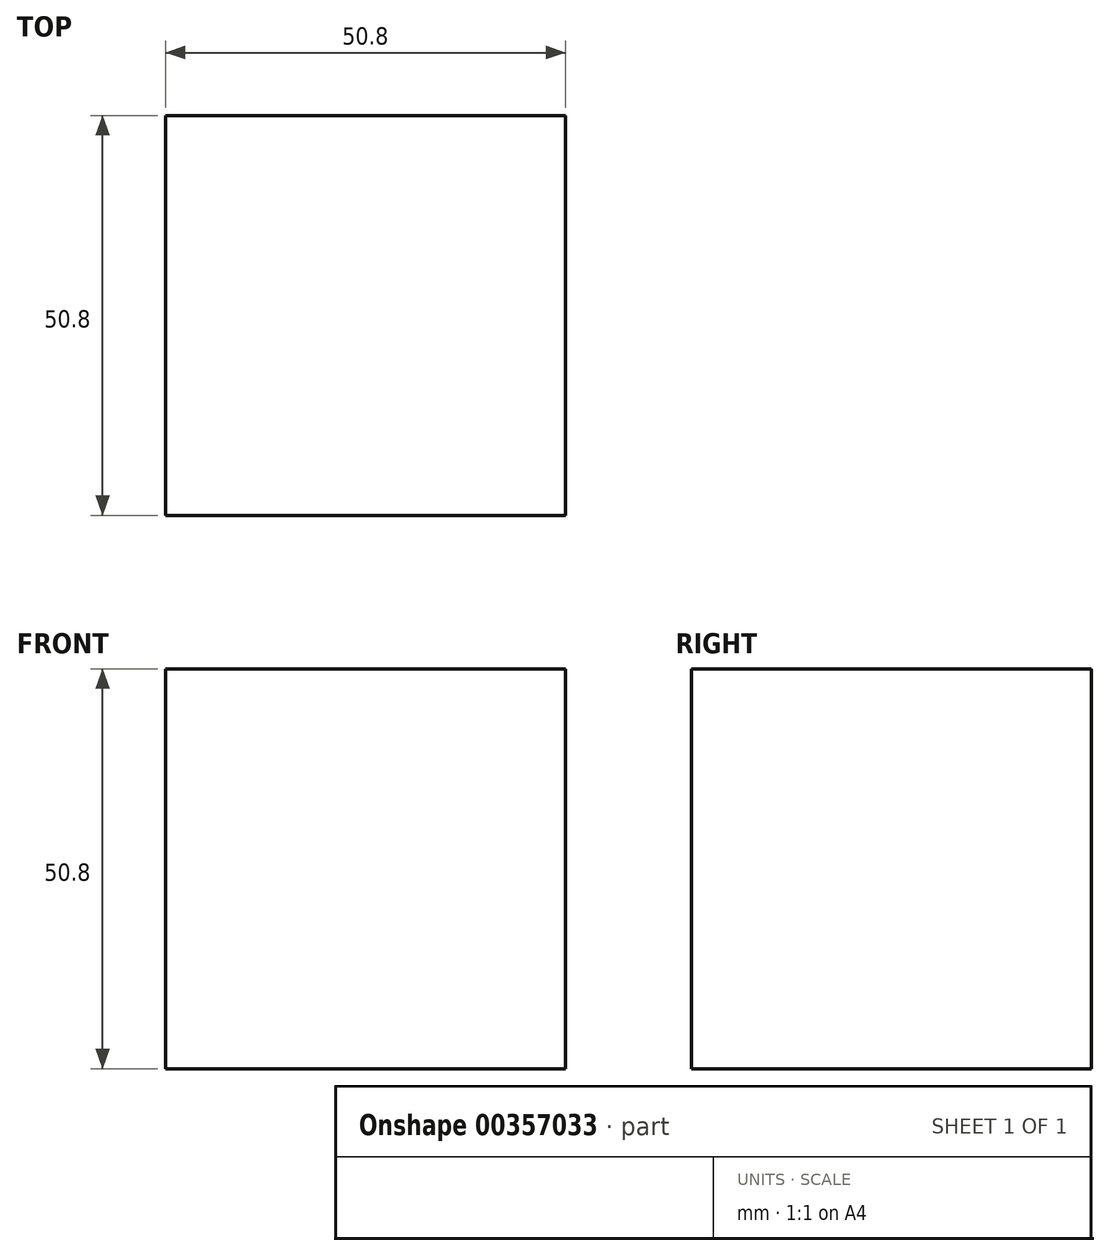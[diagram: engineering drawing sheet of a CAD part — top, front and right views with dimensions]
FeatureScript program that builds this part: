
annotation { "Feature Type Name" : "Feature", "Feature Type Description" : "" }
export const myFeature = defineFeature(function(context is Context, id is Id, definition is map)
    precondition{}
    {
        {
            var Q0;
            Q0=qCreatedBy(makeId("Front.planeOp"),FACE);
            var sketch = newSketch(context, id + "F0", { "sketchPlane" : qUnion([Q0])});
            skLineSegment(sketch, "E0", {"start": v(0, 0) * mm, "end": v(0, 50.8) * mm});
            skLineSegment(sketch, "E1", {"start": v(50.8, 50.8) * mm, "end": v(0, 50.8) * mm});
            skLineSegment(sketch, "E2", {"start": v(50.8, 50.8) * mm, "end": v(50.8, 0) * mm});
            skLineSegment(sketch, "E3", {"start": v(50.8, 0) * mm, "end": v(0, 0) * mm});
            skSolve(sketch);
        }
        {
            var Q0;
            Q0 = qSketchRegion(id + "F0", true);
            extrude(context, id + "F1", {"entities" : qUnion([Q0]), "depth" : 50.8 * mm});
        }
    });
